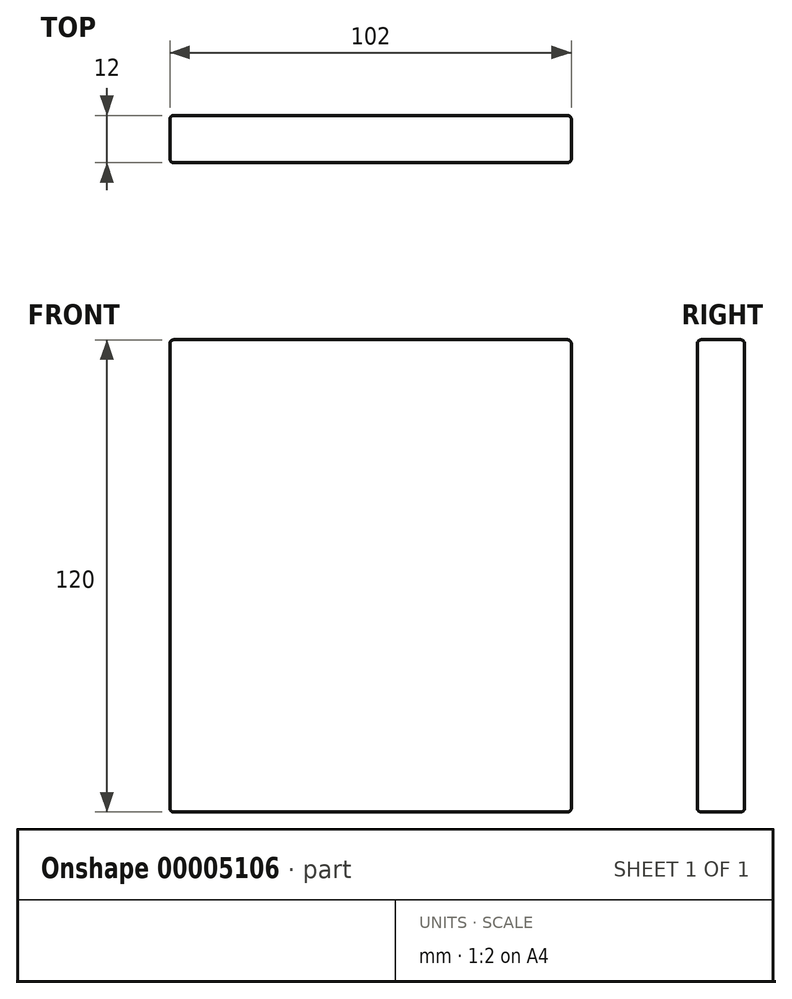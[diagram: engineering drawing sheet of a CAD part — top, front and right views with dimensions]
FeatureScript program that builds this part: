
annotation { "Feature Type Name" : "Feature", "Feature Type Description" : "" }
export const myFeature = defineFeature(function(context is Context, id is Id, definition is map)
    precondition{}
    {
        {
            var Q0;
            Q0=qCreatedBy(makeId("Front.planeOp"),FACE);
            var sketch = newSketch(context, id + "F0", { "sketchPlane" : qUnion([Q0])});
            skLineSegment(sketch, "E0.bottom", {"start": v(-68.5, 95.07) * mm, "end": v(33.5, 95.07) * mm});
            skLineSegment(sketch, "E0.top", {"start": v(-68.5, -24.93) * mm, "end": v(33.5, -24.93) * mm});
            skLineSegment(sketch, "E0.left", {"start": v(-68.5, 95.07) * mm, "end": v(-68.5, -24.93) * mm});
            skLineSegment(sketch, "E0.right", {"start": v(33.5, 95.07) * mm, "end": v(33.5, -24.93) * mm});
            skSolve(sketch);
        }
        {
            var Q0;
            Q0=makeQuery(id+"F0.imprint","IMPRINT",FACE,{"disambiguationData":[TD([[makeQuery(id+"F0.imprint","IMPRINT",EDGE,{"derivedFrom":sQuery(id+"F0.wireOp",EDGE,"E0.bottom")}),-1.0]])]});
            extrude(context, id + "F1", {"entities" : qUnion([Q0]), "depth" : 12 * mm});
        }
        {
            var Q0;
            Q0=makeQuery(id+"F1.opExtrude","CAP_EDGE",EDGE,{"disambiguationData":[OSD([sQuery(id+"F0.wireOp",EDGE,"E0.bottom")])],"isStart":false});
            var Q1;
            Q1=makeQuery(id+"F1.opExtrude","CAP_EDGE",EDGE,{"disambiguationData":[OSD([sQuery(id+"F0.wireOp",EDGE,"E0.right")])],"isStart":false});
            var Q2;
            Q2=makeQuery(id+"F1.opExtrude","SWEPT_FACE",FACE,{"disambiguationData":[OSD([sQuery(id+"F0.wireOp",EDGE,"E0.bottom")])]});
            var Q3;
            Q3=makeQuery(id+"F1.opExtrude","SWEPT_EDGE",EDGE,{"disambiguationData":[OSD([sQuery(id+"F0.wireOp",EDGE,"E0.bottom"),sQuery(id+"F0.wireOp",EDGE,"E0.right")])]});
            var Q4;
            Q4=makeQuery(id+"F1.opExtrude","CAP_EDGE",EDGE,{"disambiguationData":[OSD([sQuery(id+"F0.wireOp",EDGE,"E0.right")])],"isStart":true});
            var Q5;
            Q5=makeQuery(id+"F1.opExtrude","CAP_EDGE",EDGE,{"disambiguationData":[OSD([sQuery(id+"F0.wireOp",EDGE,"E0.bottom")])],"isStart":true});
            var Q6;
            Q6=makeQuery(id+"F1.opExtrude","SWEPT_EDGE",EDGE,{"disambiguationData":[OSD([sQuery(id+"F0.wireOp",EDGE,"E0.top"),sQuery(id+"F0.wireOp",EDGE,"E0.right")])]});
            var Q7;
            Q7=makeQuery(id+"F1.opExtrude","CAP_EDGE",EDGE,{"disambiguationData":[OSD([sQuery(id+"F0.wireOp",EDGE,"E0.top")])],"isStart":false});
            var Q8;
            Q8=makeQuery(id+"F1.opExtrude","CAP_EDGE",EDGE,{"disambiguationData":[OSD([sQuery(id+"F0.wireOp",EDGE,"E0.left")])],"isStart":false});
            var Q9;
            Q9=makeQuery(id+"F1.opExtrude","SWEPT_EDGE",EDGE,{"disambiguationData":[OSD([sQuery(id+"F0.wireOp",EDGE,"E0.bottom"),sQuery(id+"F0.wireOp",EDGE,"E0.left")])]});
            var Q10;
            Q10=makeQuery(id+"F1.opExtrude","SWEPT_FACE",FACE,{"disambiguationData":[OSD([sQuery(id+"F0.wireOp",EDGE,"E0.left")])]});
            var Q11;
            Q11=makeQuery(id+"F1.opExtrude","CAP_EDGE",EDGE,{"disambiguationData":[OSD([sQuery(id+"F0.wireOp",EDGE,"E0.left")])],"isStart":true});
            var Q12;
            Q12=makeQuery(id+"F1.opExtrude","CAP_EDGE",EDGE,{"disambiguationData":[OSD([sQuery(id+"F0.wireOp",EDGE,"E0.top")])],"isStart":true});
            fillet(context, id + "F2", {"entities" : qUnion([Q0, Q1, Q2, Q3, Q4, Q5, Q6, Q7, Q8, Q9, Q10, Q11, Q12]), "radius" : 1 * mm, "tangentPropagation" : true, "allowEdgeOverflow" : false});
        }
    });
